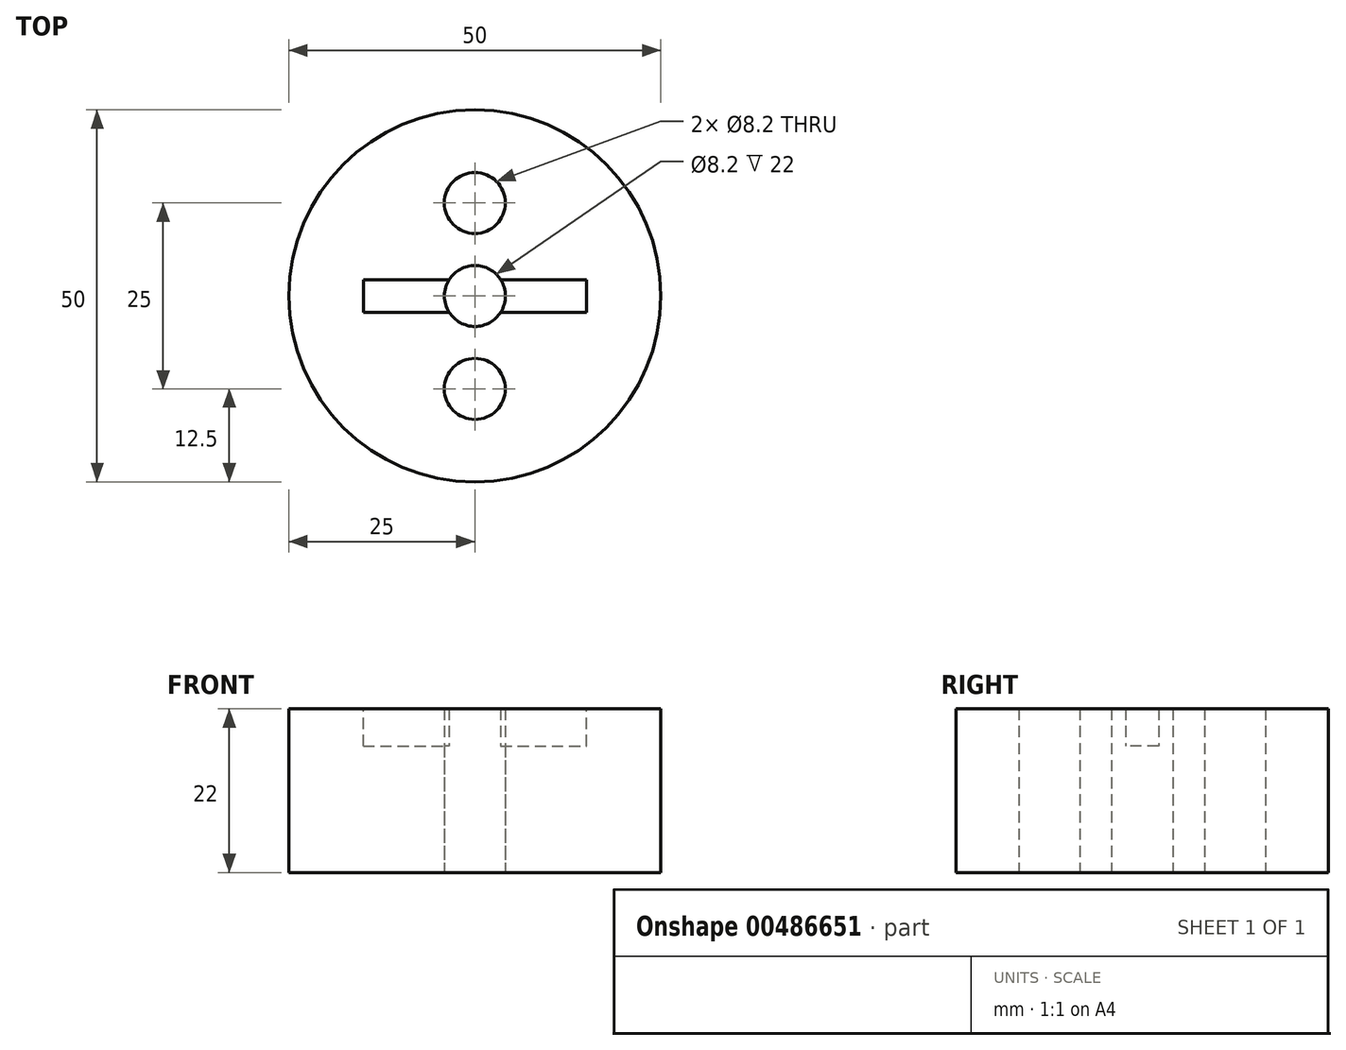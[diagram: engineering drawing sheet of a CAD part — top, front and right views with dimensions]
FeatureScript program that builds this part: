
annotation { "Feature Type Name" : "Feature", "Feature Type Description" : "" }
export const myFeature = defineFeature(function(context is Context, id is Id, definition is map)
    precondition{}
    {
        {
            var Q0;
            Q0=qCreatedBy(makeId("Top.planeOp"),FACE);
            var sketch = newSketch(context, id + "F0", { "sketchPlane" : qUnion([Q0])});
            skCircle(sketch, "E0", {"center": v(0, 0) * mm, "radius": 25 * mm});
            skCircle(sketch, "E1", {"center": v(0, 0) * mm, "radius": 4.1 * mm});
            skCircle(sketch, "E2", {"center": v(0, 12.5) * mm, "radius": 4.1 * mm});
            skCircle(sketch, "E3.MirrorC", {"center": v(0, -12.5) * mm, "radius": 4.1 * mm});
            skSolve(sketch);
        }
        {
            var Q0;
            Q0 = qSketchRegion(id + "F0", true);
            extrude(context, id + "F1", {"entities" : qUnion([Q0]), "depth" : 22 * mm});
        }
        {
            var Q0;
            Q0=makeQuery(id+"F1.opExtrude","CAP_FACE",FACE,{"disambiguationData":[OSD([sQuery(id+"F0.wireOp",EDGE,"E0"),sQuery(id+"F0.wireOp",EDGE,"E1")])],"isStart":false});
            var sketch = newSketch(context, id + "F2", { "sketchPlane" : qUnion([Q0])});
            skLineSegment(sketch, "E4.bottom", {"start": v(-15, 2.2) * mm, "end": v(15, 2.2) * mm});
            skLineSegment(sketch, "E4.top", {"start": v(-15, -2.2) * mm, "end": v(15, -2.2) * mm});
            skLineSegment(sketch, "E4.left", {"start": v(-15, 2.2) * mm, "end": v(-15, -2.2) * mm});
            skLineSegment(sketch, "E4.right", {"start": v(15, 2.2) * mm, "end": v(15, -2.2) * mm});
            skSolve(sketch);
        }
        {
            var Q0;
            Q0 = qSketchRegion(id + "F2", true);
            extrude(context, id + "F3", {"entities" : qUnion([Q0]), "operationType" : NewBodyOperationType.REMOVE, "oppositeDirection" : true, "depth" : 5 * mm});
        }
    });
